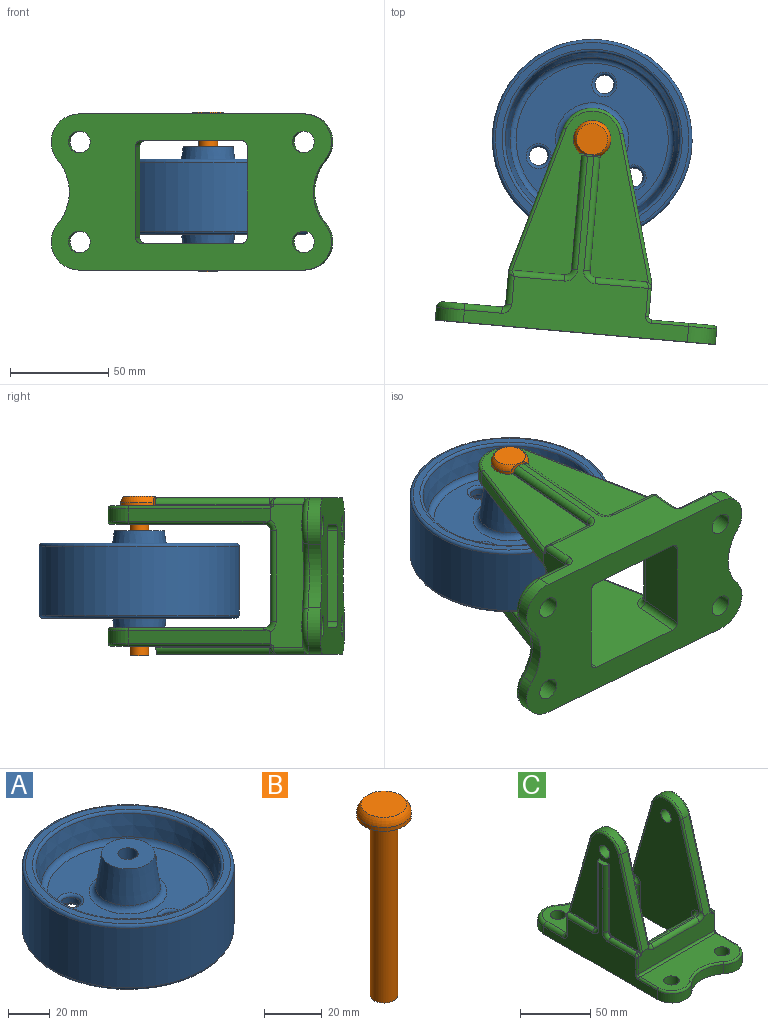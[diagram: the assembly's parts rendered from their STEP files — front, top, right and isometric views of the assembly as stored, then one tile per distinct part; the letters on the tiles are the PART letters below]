
ASSEMBLY  parts=3 mates=2
PART A: 29 faces, bbox 110x110x50.8 mm
  f0: plane 25.4x25.4mm, normal (0,0,1), area 433.5mm2, adj f1,f11
  f1: cone r=12.7mm half-angle=8.1deg, axis (0,0,-1), area 1744.1mm2, adj f0,f12
  f2: plane 77.34x77.34mm, normal (0,0,1), area 3228.1mm2, adj f12,f13,f24,f26,f28
  f3: cone r=44.45mm half-angle=11.3deg, axis (0,0,1), area 3318.4mm2, adj f13,f16
  f4: plane 98.43x98.43mm, normal (0,0,1), area 1032.6mm2, adj f16,f17
  f5: cylinder r=50.8mm len=101.6mm, axis (0,0,1), area 11147.6mm2, adj f17,f18
  f6: plane 98.43x98.43mm, normal (0,0,-1), area 1032.6mm2, adj f18,f19
  f7: cone r=41.27mm half-angle=11.3deg, axis (0,0,-1), area 3318.4mm2, adj f14,f19
  f8: plane 77.34x77.34mm, normal (0,0,-1), area 3228.1mm2, adj f14,f15,f23,f25,f27
  f9: cone r=15.88mm half-angle=8.1deg, axis (0,0,1), area 1744.1mm2, adj f10,f15
  f10: plane 25.4x25.4mm, normal (0,0,-1), area 433.5mm2, adj f9,f11
  f11: cylinder r=4.83mm len=50.8mm, axis (0,0,1), area 1540.4mm2, adj f0,f10
  f12: torus R=18.63mm, axis (0,0,-1), area 476.6mm2, adj f1,f2
  f13: torus R=38.67mm, axis (0,0,-1), area 1110.5mm2, adj f2,f3
  f14: torus R=38.67mm, axis (0,0,-1), area 1110.5mm2, adj f7,f8
  f15: torus R=18.63mm, axis (0,0,-1), area 476.6mm2, adj f8,f9
  f16: torus R=45.75mm, axis (0,0,1), area 614mm2, adj f3,f4
  f17: torus R=49.21mm, axis (0,0,1), area 786.9mm2, adj f4,f5
  f18: torus R=49.21mm, axis (0,0,1), area 786.9mm2, adj f5,f6
  f19: torus R=45.75mm, axis (0,0,1), area 614mm2, adj f6,f7
  f20: cylinder r=4.76mm len=9.53mm, axis (0,0,-1), area 95mm2, adj f23,f24
  f21: cylinder r=4.76mm len=9.53mm, axis (0,0,-1), area 95mm2, adj f25,f26
  f22: cylinder r=4.76mm len=9.53mm, axis (0,0,-1), area 95mm2, adj f27,f28
  f23: torus R=6.35mm, axis (0,0,-1), area 83.7mm2, adj f8,f20
  f24: torus R=6.35mm, axis (0,0,-1), area 83.7mm2, adj f2,f20
  f25: torus R=6.35mm, axis (0,0,-1), area 83.7mm2, adj f8,f21
  f26: torus R=6.35mm, axis (0,0,-1), area 83.7mm2, adj f2,f21
  f27: torus R=6.35mm, axis (0,0,-1), area 83.7mm2, adj f8,f22
  f28: torus R=6.35mm, axis (0,0,-1), area 83.7mm2, adj f2,f22
PART B: 7 faces, bbox 19.1x19.1x81 mm
  f0: plane 9.53x9.53mm, normal (0,0,-1), area 71.3mm2, adj f1
  f1: cylinder r=4.76mm len=76.19mm, axis (0,0,1), area 2279.8mm2, adj f0,f2
  f2: plane 19.05x17.46mm, normal (0,0,-1), area 202.4mm2, adj f1,f3,f6
  f3: cylinder r=9.53mm len=19.05mm, axis (0,0,1), area 77.3mm2, adj f2,f4,f6
  f4: torus R=4.02mm, axis (0,0,1), area 172.9mm2, adj f3,f5,f6
  f5: plane 15.88x15.88mm, normal (0,0,1), area 197.9mm2, adj f4
  f6: plane 10.54x4.76mm, normal (1,0,0), area 42.1mm2, adj f2,f3,f4
PART C: 123 faces, bbox 83.1x146.6x117 mm
  f0: plane 77.61x18.87mm, normal (0,-1,0), area 1144.7mm2, adj f30,f32,f61,f63,f68,f71,f87,f90
  f1: plane 84.6x69.86mm, normal (-1,0,0), area 3125.5mm2, adj f3,f28,f34,f36,f37,f38,f59,f60
  f2: plane 28.58x0.8mm, normal (0,0,1), area 22.7mm2, adj f6,f58,f72,f85,f97
  f3: plane 25.4x0.79mm, normal (0,0,1), area 20.2mm2, adj f1,f60,f114,f116
  f4: plane 112.71x67.63mm, normal (1,0,0), area 5123.1mm2, adj f26,f34,f43,f44,f45,f50,f51,f52
  f5: plane 112.71x67.63mm, normal (-1,0,0), area 5123.1mm2, adj f26,f42,f46,f48,f49,f54,f55,f56
  f6: plane 84.14x69.72mm, normal (1,0,0), area 3125.3mm2, adj f2,f8,f39,f40,f41,f42,f57,f58
  f7: plane 46.04x1.59mm, normal (0,0,1), area 73.1mm2, adj f51,f53,f54,f121
  f8: plane 25.39x0.8mm, normal (0,0,1), area 20.2mm2, adj f6,f57,f61,f87,f93
  f9: plane 46.04x1.59mm, normal (0,0,1), area 73.1mm2, adj f43,f46,f47,f118
  f10: plane 73.03x30.16mm, normal (0,0,1), area 1684.4mm2, adj f20,f21,f73,f101,f102,f103,f104,f105
  f11: cylinder r=14.29mm len=23.43mm, axis (0,0,-1), area 205.5mm2, adj f12,f24,f26,f104
  f12: plane 114.3x89.69mm, normal (-1,0,0), area 2289.9mm2, adj f11,f13,f26,f38,f69,f70,f71,f105
  f13: cylinder r=14.29mm len=23.43mm, axis (0,0,-1), area 256.9mm2, adj f12,f14,f26,f67
  f14: cylinder r=25.4mm len=32.51mm, axis (0,0,-1), area 280mm2, adj f13,f15,f26,f65
  f15: cylinder r=14.29mm len=23.43mm, axis (0,0,-1), area 256.9mm2, adj f14,f16,f26,f62
  f16: plane 114.3x89.69mm, normal (1,0,0), area 2289.9mm2, adj f15,f17,f26,f41,f63,f64,f66,f91
  f17: cylinder r=14.29mm len=23.43mm, axis (0,0,-1), area 205.5mm2, adj f16,f24,f26,f102
  f18: plane 46.04x25.4mm, normal (0,-1,0), area 1169.4mm2, adj f26,f50,f53,f56
  f19: plane 46.04x25.4mm, normal (0,1,0), area 1169.4mm2, adj f26,f44,f47,f49
  f20: cylinder r=5.56mm len=11.11mm, axis (0,0,-1), area 332.5mm2, adj f10,f26
  f21: cylinder r=5.56mm len=11.11mm, axis (0,0,-1), area 332.5mm2, adj f10,f26
  f22: cylinder r=5.56mm len=11.11mm, axis (0,0,-1), area 332.5mm2, adj f25,f26
  f23: cylinder r=5.56mm len=11.11mm, axis (0,0,-1), area 332.5mm2, adj f25,f26
  f24: cylinder r=25.4mm len=32.51mm, axis (0,0,-1), area 224mm2, adj f11,f17,f26,f103
  f25: plane 76.2x31.75mm, normal (0,0,1), area 1891.8mm2, adj f22,f23,f62,f64,f65,f67,f68,f69
  f26: plane 142.88x79.38mm, normal (0,0,-1), area 7277.2mm2, adj f4,f5,f11,f12,f13,f14,f15,f16
  f27: plane 73.03x17.46mm, normal (0,1,0), area 1099.1mm2, adj f29,f31,f72,f73,f74,f85,f88,f99
  f28: plane 26.99x0.8mm, normal (0,0,1), area 21.4mm2, adj f1,f59,f74,f88,f109
  f29: plane 74.22x21.25mm, normal (0,0.96,0.28), area 490.7mm2, adj f27,f35,f78,f79,f85,f120
  f30: plane 74.22x21.25mm, normal (0,-0.96,0.28), area 490.7mm2, adj f0,f35,f75,f76,f87,f117
  f31: plane 74.22x21.25mm, normal (0,0.96,0.28), area 490.7mm2, adj f27,f33,f80,f81,f88,f122
  f32: plane 74.22x21.25mm, normal (0,-0.96,0.28), area 490.7mm2, adj f0,f33,f83,f84,f90,f119
  f33: cylinder r=15.88mm len=30.52mm, axis (-1,0,0), area 260.5mm2, adj f31,f32,f82,f89
  f34: cylinder r=5.16mm len=10.32mm, axis (-1,0,0), area 308.8mm2, adj f1,f4
  f35: cylinder r=15.88mm len=30.52mm, axis (1,0,0), area 260.5mm2, adj f29,f30,f77,f86
  f36: plane 57.94x0.79mm, normal (0,1,0), area 46mm2, adj f1,f38,f59,f111
  f37: plane 57.94x0.79mm, normal (0,-1,0), area 46mm2, adj f1,f38,f60,f112
  f38: plane 9.53x3.97mm, normal (0,0,1), area 33.5mm2, adj f1,f12,f36,f37,f111,f112
  f39: plane 57.94x0.79mm, normal (0,1,0), area 46mm2, adj f6,f41,f58,f95
  f40: plane 57.94x0.79mm, normal (0,-1,0), area 46mm2, adj f6,f41,f57,f91
  f41: plane 9.53x3.97mm, normal (0,0,1), area 33.5mm2, adj f6,f16,f39,f40,f91,f95
  f42: cylinder r=5.16mm len=10.32mm, axis (-1,0,0), area 308.8mm2, adj f5,f6
  f43: cylinder r=3.17mm len=3.18mm, axis (0,1,0), area 7.9mm2, adj f4,f9,f45,f119
  f44: cylinder r=3.17mm len=25.4mm, axis (0,0,1), area 126.7mm2, adj f4,f19,f26,f45
  f45: torus R=6.35mm, axis (1,0,0), area 33.9mm2, adj f4,f43,f44,f47
  f46: cylinder r=3.17mm len=3.18mm, axis (0,-1,0), area 7.9mm2, adj f5,f9,f48,f117
  f47: cylinder r=3.17mm len=46.04mm, axis (1,0,0), area 229.6mm2, adj f9,f19,f45,f48
  f48: torus R=6.35mm, axis (1,0,0), area 33.9mm2, adj f5,f46,f47,f49
  f49: cylinder r=3.17mm len=25.4mm, axis (0,0,-1), area 126.7mm2, adj f5,f19,f26,f48
  f50: cylinder r=3.17mm len=25.4mm, axis (0,0,-1), area 126.7mm2, adj f4,f18,f26,f52
  f51: cylinder r=3.17mm len=3.18mm, axis (0,1,0), area 7.9mm2, adj f4,f7,f52,f122
  f52: torus R=6.35mm, axis (1,0,0), area 33.9mm2, adj f4,f50,f51,f53
  f53: cylinder r=3.17mm len=46.04mm, axis (-1,0,0), area 229.6mm2, adj f7,f18,f52,f55
  f54: cylinder r=3.17mm len=3.18mm, axis (0,-1,0), area 7.9mm2, adj f5,f7,f55,f120
  f55: torus R=6.35mm, axis (1,0,0), area 33.9mm2, adj f5,f53,f54,f56
  f56: cylinder r=3.17mm len=25.4mm, axis (0,0,1), area 126.7mm2, adj f5,f18,f26,f55
  f57: cylinder r=3.17mm len=3.18mm, axis (1,0,0), area 4mm2, adj f6,f8,f40,f92
  f58: cylinder r=3.17mm len=3.18mm, axis (-1,0,0), area 4mm2, adj f2,f6,f39,f96
  f59: cylinder r=3.17mm len=3.18mm, axis (-1,0,0), area 4mm2, adj f1,f28,f36,f110
  f60: cylinder r=3.17mm len=3.18mm, axis (1,0,0), area 4mm2, adj f1,f3,f37,f113
  f61: cylinder r=1.59mm len=1.59mm, axis (-1,0,0), area 2.6mm2, adj f0,f8,f87,f94
  f62: torus R=12.7mm, axis (0,0,1), area 77.4mm2, adj f15,f25,f64,f65
  f63: cylinder r=1.59mm len=14.29mm, axis (0,0,1), area 35.6mm2, adj f0,f16,f66,f94
  f64: cylinder r=1.59mm len=19.05mm, axis (0,-1,0), area 47.5mm2, adj f16,f25,f62,f66
  f65: torus R=26.99mm, axis (0,0,1), area 90mm2, adj f14,f25,f62,f67
  f66: torus R=3.17mm, axis (1,0,0), area 8.5mm2, adj f16,f63,f64,f68
  f67: torus R=12.7mm, axis (0,0,1), area 77.4mm2, adj f13,f25,f65,f69
  f68: cylinder r=1.59mm len=76.2mm, axis (1,0,0), area 190mm2, adj f0,f25,f66,f70
  f69: cylinder r=1.59mm len=19.05mm, axis (0,1,0), area 47.5mm2, adj f12,f25,f67,f70
  f70: torus R=3.17mm, axis (1,0,0), area 8.5mm2, adj f12,f68,f69,f71
  f71: cylinder r=1.59mm len=14.29mm, axis (0,0,-1), area 35.6mm2, adj f0,f12,f70,f115
  f72: cylinder r=1.59mm len=1.59mm, axis (1,0,0), area 2.6mm2, adj f2,f27,f85,f98
  f73: cylinder r=1.59mm len=73.03mm, axis (-1,0,0), area 182.1mm2, adj f10,f27,f100,f106
  f74: cylinder r=1.59mm len=1.59mm, axis (1,0,0), area 2.6mm2, adj f27,f28,f88,f108
  f75: bspline ~1.81x1.32mm, area 1mm2, adj f30,f76,f117
  f76: cylinder r=1.59mm len=71.04mm, axis (0,0.28,0.96), area 182.8mm2, adj f5,f30,f75,f77,f117
  f77: torus R=14.29mm, axis (1,0,0), area 98.6mm2, adj f5,f35,f76,f78
  f78: cylinder r=1.59mm len=71.04mm, axis (0,0.28,-0.96), area 182.8mm2, adj f5,f29,f77,f79,f120
  f79: bspline ~2.22x2.16mm, area 1mm2, adj f29,f78,f120
  f80: bspline ~1.81x1.32mm, area 1mm2, adj f31,f81,f122
  f81: cylinder r=1.59mm len=71.04mm, axis (0,-0.28,0.96), area 182.8mm2, adj f4,f31,f80,f82,f122
  f82: torus R=14.29mm, axis (1,0,0), area 98.6mm2, adj f4,f33,f81,f83
  f83: cylinder r=1.59mm len=71.04mm, axis (0,-0.28,-0.96), area 182.8mm2, adj f4,f32,f82,f84,f119
  f84: bspline ~2.22x2.16mm, area 1mm2, adj f32,f83,f119
  f85: cylinder r=1.59mm len=76.12mm, axis (0,-0.28,0.96), area 193mm2, adj f2,f6,f27,f29,f72,f86
  f86: torus R=14.29mm, axis (1,0,0), area 98.6mm2, adj f6,f35,f85,f87
  f87: cylinder r=1.59mm len=76.12mm, axis (0,-0.28,-0.96), area 193mm2, adj f0,f6,f8,f30,f61,f86
  f88: cylinder r=1.59mm len=76.12mm, axis (0,-0.28,0.96), area 193mm2, adj f1,f27,f28,f31,f74,f89
  f89: torus R=14.29mm, axis (1,0,0), area 98.6mm2, adj f1,f33,f88,f90
  f90: cylinder r=1.59mm len=77.59mm, axis (0,-0.28,-0.96), area 195.4mm2, adj f0,f1,f32,f89,f116
  f91: cylinder r=3.17mm len=57.94mm, axis (0,0,1), area 288.9mm2, adj f16,f40,f41,f92
  f92: torus R=6.35mm, axis (1,0,0), area 33.9mm2, adj f16,f57,f91,f93
  f93: cylinder r=3.17mm len=25.39mm, axis (0,-1,0), area 126.6mm2, adj f8,f16,f92,f94
  f94: torus R=1.59mm, axis (0,1,0), area 10.2mm2, adj f0,f61,f63,f93
  f95: cylinder r=3.17mm len=57.94mm, axis (0,0,-1), area 288.9mm2, adj f16,f39,f41,f96
  f96: torus R=6.35mm, axis (1,0,0), area 33.9mm2, adj f16,f58,f95,f97
  f97: cylinder r=3.17mm len=28.58mm, axis (0,-1,0), area 138.6mm2, adj f2,f16,f96,f98
  f98: bspline ~3.33x3.18mm, area 5.5mm2, adj f72,f97,f99
  f99: cylinder r=3.17mm len=15.88mm, axis (0,0,-1), area 75.2mm2, adj f16,f27,f98,f100
  f100: torus R=4.76mm, axis (1,0,0), area 21.5mm2, adj f16,f73,f99,f101
  f101: cylinder r=3.17mm len=19.05mm, axis (0,-1,0), area 95mm2, adj f10,f16,f100,f102
  f102: torus R=11.11mm, axis (0,0,1), area 148.4mm2, adj f10,f17,f101,f103
  f103: torus R=28.57mm, axis (0,0,1), area 183.9mm2, adj f10,f24,f102,f104
  f104: torus R=11.11mm, axis (0,0,1), area 148.4mm2, adj f10,f11,f103,f105
  f105: cylinder r=3.17mm len=19.05mm, axis (0,1,0), area 95mm2, adj f10,f12,f104,f106
  f106: torus R=4.76mm, axis (1,0,0), area 21.5mm2, adj f12,f73,f105,f107
  f107: cylinder r=3.17mm len=15.88mm, axis (0,0,1), area 75.2mm2, adj f12,f27,f106,f108
  f108: bspline ~3.33x3.18mm, area 5.5mm2, adj f74,f107,f109
  f109: cylinder r=3.17mm len=26.99mm, axis (0,1,0), area 130.6mm2, adj f12,f28,f108,f110
  f110: torus R=6.35mm, axis (1,0,0), area 33.9mm2, adj f12,f59,f109,f111
  f111: cylinder r=3.17mm len=57.94mm, axis (0,0,-1), area 288.9mm2, adj f12,f36,f38,f110
  f112: cylinder r=3.17mm len=57.94mm, axis (0,0,1), area 288.9mm2, adj f12,f37,f38,f113
  f113: torus R=6.35mm, axis (1,0,0), area 33.9mm2, adj f12,f60,f112,f114
  f114: cylinder r=3.17mm len=26.99mm, axis (0,1,0), area 130.6mm2, adj f3,f12,f113,f115
  f115: bspline ~3.33x3.18mm, area 5.5mm2, adj f71,f114,f116
  f116: cylinder r=3.17mm len=3.18mm, axis (-1,0,0), area 8.2mm2, adj f0,f1,f3,f90,f115
  f117: torus R=6.35mm, axis (0,1,0), area 29.2mm2, adj f0,f5,f30,f46,f75,f76,f118
  f118: cylinder r=3.17mm len=46.04mm, axis (-1,0,0), area 229.6mm2, adj f0,f9,f117,f119
  f119: torus R=6.35mm, axis (0,1,0), area 29.2mm2, adj f0,f4,f32,f43,f83,f84,f118
  f120: torus R=6.35mm, axis (0,1,0), area 29.2mm2, adj f5,f27,f29,f54,f78,f79,f121
  f121: cylinder r=3.17mm len=46.04mm, axis (1,0,0), area 229.6mm2, adj f7,f27,f120,f122
  f122: torus R=6.35mm, axis (0,1,0), area 29.2mm2, adj f4,f27,f31,f51,f80,f81,f121
PLACE A rot(axis=(0,0,1),47.5deg) t=(69.88,135.26,82.53)mm
PLACE B rot(axis=(0,0,-1),97.5deg) t=(69.88,135.26,90.74)mm
PLACE C rot(axis=(-0.56,0.61,0.56),117.2deg) t=(61.31,37.21,90.73)mm
MATE revolute B.f1 <-> A.f14  axis (0,0,1) through (69.88,135.26,88.36)mm
MATE revolute C.f34 <-> B.f1  axis (0,0,1) through (69.88,135.26,126.45)mm
